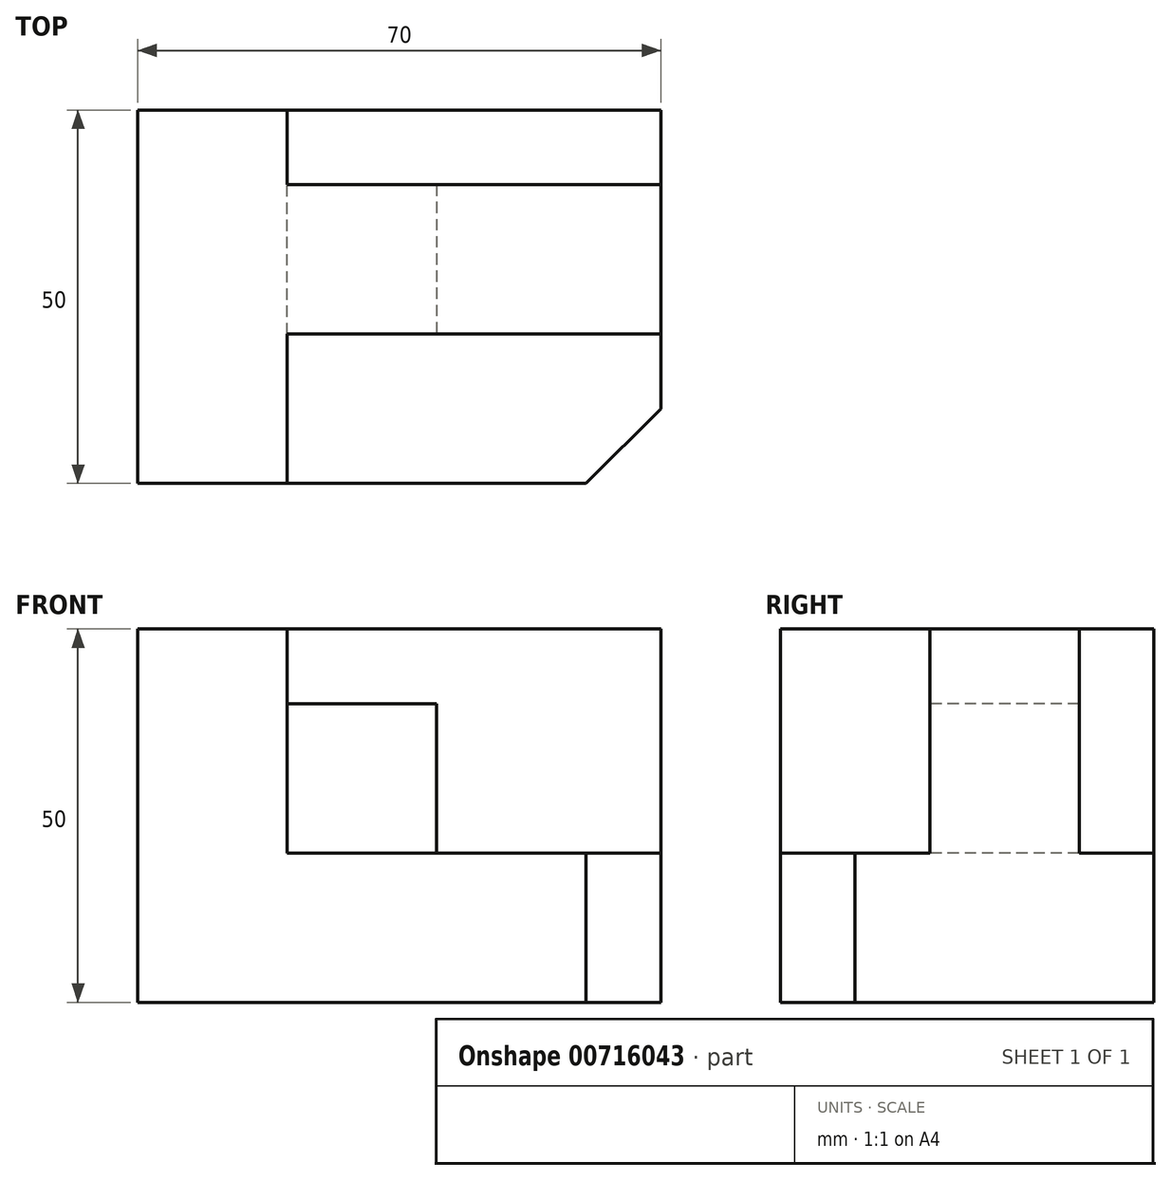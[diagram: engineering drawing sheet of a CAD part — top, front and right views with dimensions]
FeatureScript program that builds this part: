
annotation { "Feature Type Name" : "Feature", "Feature Type Description" : "" }
export const myFeature = defineFeature(function(context is Context, id is Id, definition is map)
    precondition{}
    {
        {
            var Q0;
            Q0=qCreatedBy(makeId("Top.planeOp"),FACE);
            var sketch = newSketch(context, id + "F0", { "sketchPlane" : qUnion([Q0])});
            skLineSegment(sketch, "E0.bottom", {"start": v(0, 0) * mm, "end": v(70, 0) * mm});
            skLineSegment(sketch, "E0.top", {"start": v(0, 50) * mm, "end": v(70, 50) * mm});
            skLineSegment(sketch, "E0.left", {"start": v(0, 0) * mm, "end": v(0, 50) * mm});
            skLineSegment(sketch, "E0.right", {"start": v(70, 0) * mm, "end": v(70, 50) * mm});
            skSolve(sketch);
        }
        {
            var Q0;
            Q0 = qSketchRegion(id + "F0", true);
            var Q1;
            Q1=makeQuery(id+"F0.imprint","IMPRINT",FACE,{"disambiguationData":[TD([[makeQuery(id+"F0.imprint","IMPRINT",EDGE,{"derivedFrom":sQuery(id+"F0.wireOp",EDGE,"E0.bottom")}),1.0]])]});
            extrude(context, id + "F1", {"entities" : qUnion([Q0, Q1]), "depth" : 50 * mm, "offsetDistance" : 25 * mm});
        }
        {
            var Q0;
            Q0=makeQuery(id+"F1.opExtrude","CAP_FACE",FACE,{"disambiguationData":[OSD([sQuery(id+"F0.wireOp",EDGE,"E0.bottom"),sQuery(id+"F0.wireOp",EDGE,"E0.top"),sQuery(id+"F0.wireOp",EDGE,"E0.left"),sQuery(id+"F0.wireOp",EDGE,"E0.right")])],"isStart":false});
            var sketch = newSketch(context, id + "F2", { "sketchPlane" : qUnion([Q0])});
            skLineSegment(sketch, "E1.bottom", {"start": v(70, 0) * mm, "end": v(20, 0) * mm});
            skLineSegment(sketch, "E1.top", {"start": v(70, 20) * mm, "end": v(20, 20) * mm});
            skLineSegment(sketch, "E1.left", {"start": v(70, 0) * mm, "end": v(70, 20) * mm});
            skLineSegment(sketch, "E1.right", {"start": v(20, 0) * mm, "end": v(20, 20) * mm});
            skSolve(sketch);
        }
        {
            var Q0;
            Q0 = qSketchRegion(id + "F2", true);
            extrude(context, id + "F3", {"entities" : qUnion([Q0]), "operationType" : NewBodyOperationType.REMOVE, "oppositeDirection" : true, "depth" : 30 * mm, "offsetDistance" : 25 * mm});
        }
        {
            var Q0;
            Q0=makeQuery(id+"F1.opExtrude","CAP_FACE",FACE,{"disambiguationData":[OSD([sQuery(id+"F0.wireOp",EDGE,"E0.bottom"),sQuery(id+"F0.wireOp",EDGE,"E0.top"),sQuery(id+"F0.wireOp",EDGE,"E0.left"),sQuery(id+"F0.wireOp",EDGE,"E0.right")])],"isStart":false});
            var sketch = newSketch(context, id + "F4", { "sketchPlane" : qUnion([Q0])});
            skLineSegment(sketch, "E2.bottom", {"start": v(70, 50) * mm, "end": v(20, 50) * mm});
            skLineSegment(sketch, "E2.top", {"start": v(70, 40) * mm, "end": v(20, 40) * mm});
            skLineSegment(sketch, "E2.left", {"start": v(70, 50) * mm, "end": v(70, 40) * mm});
            skLineSegment(sketch, "E2.right", {"start": v(20, 50) * mm, "end": v(20, 40) * mm});
            skSolve(sketch);
        }
        {
            var Q0;
            Q0=makeQuery(id+"F4.imprint","IMPRINT",FACE,{"disambiguationData":[TD([[makeQuery(id+"F4.imprint","IMPRINT",EDGE,{"derivedFrom":sQuery(id+"F4.wireOp",EDGE,"E2.bottom")}),-1.0]])]});
            extrude(context, id + "F5", {"entities" : qUnion([Q0]), "operationType" : NewBodyOperationType.REMOVE, "oppositeDirection" : true, "depth" : 30 * mm, "offsetDistance" : 25 * mm});
        }
        {
            var Q0;
            Q0=makeQuery(id+"F3.boolean.opBoolean","COPY",FACE,{"derivedFrom":makeQuery(id+"F3.opExtrude","SWEPT_FACE",FACE,{"disambiguationData":[OSD([sQuery(id+"F2.wireOp",EDGE,"E1.top")])]})});
            var sketch = newSketch(context, id + "F6", { "sketchPlane" : qUnion([Q0])});
            skLineSegment(sketch, "E3.bottom", {"start": v(20, 20) * mm, "end": v(40, 20) * mm});
            skLineSegment(sketch, "E3.top", {"start": v(20, 40) * mm, "end": v(40, 40) * mm});
            skLineSegment(sketch, "E3.left", {"start": v(20, 20) * mm, "end": v(20, 40) * mm});
            skLineSegment(sketch, "E3.right", {"start": v(40, 20) * mm, "end": v(40, 40) * mm});
            skSolve(sketch);
        }
        {
            var Q0;
            Q0 = qSketchRegion(id + "F6", true);
            var Q1;
            Q1=makeQuery(id+"F6.imprint","IMPRINT",FACE,{"disambiguationData":[TD([[makeQuery(id+"F6.imprint","IMPRINT",EDGE,{"derivedFrom":sQuery(id+"F6.wireOp",EDGE,"E3.bottom")}),-1.0]])]});
            extrude(context, id + "F7", {"entities" : qUnion([Q0, Q1]), "operationType" : NewBodyOperationType.REMOVE, "endBound" : BoundingType.UP_TO_NEXT, "oppositeDirection" : true, "depth" : 25 * mm, "offsetDistance" : 25 * mm});
        }
        {
            var Q0;
            Q0=makeQuery(id+"F1.opExtrude","SWEPT_EDGE",EDGE,{"disambiguationData":[OSD([sQuery(id+"F0.wireOp",EDGE,"E0.bottom"),sQuery(id+"F0.wireOp",EDGE,"E0.right")])]});
            chamfer(context, id + "F8", {"entities" : qUnion([Q0]), "width" : 10 * mm, "tangentPropagation" : true});
        }
    });
